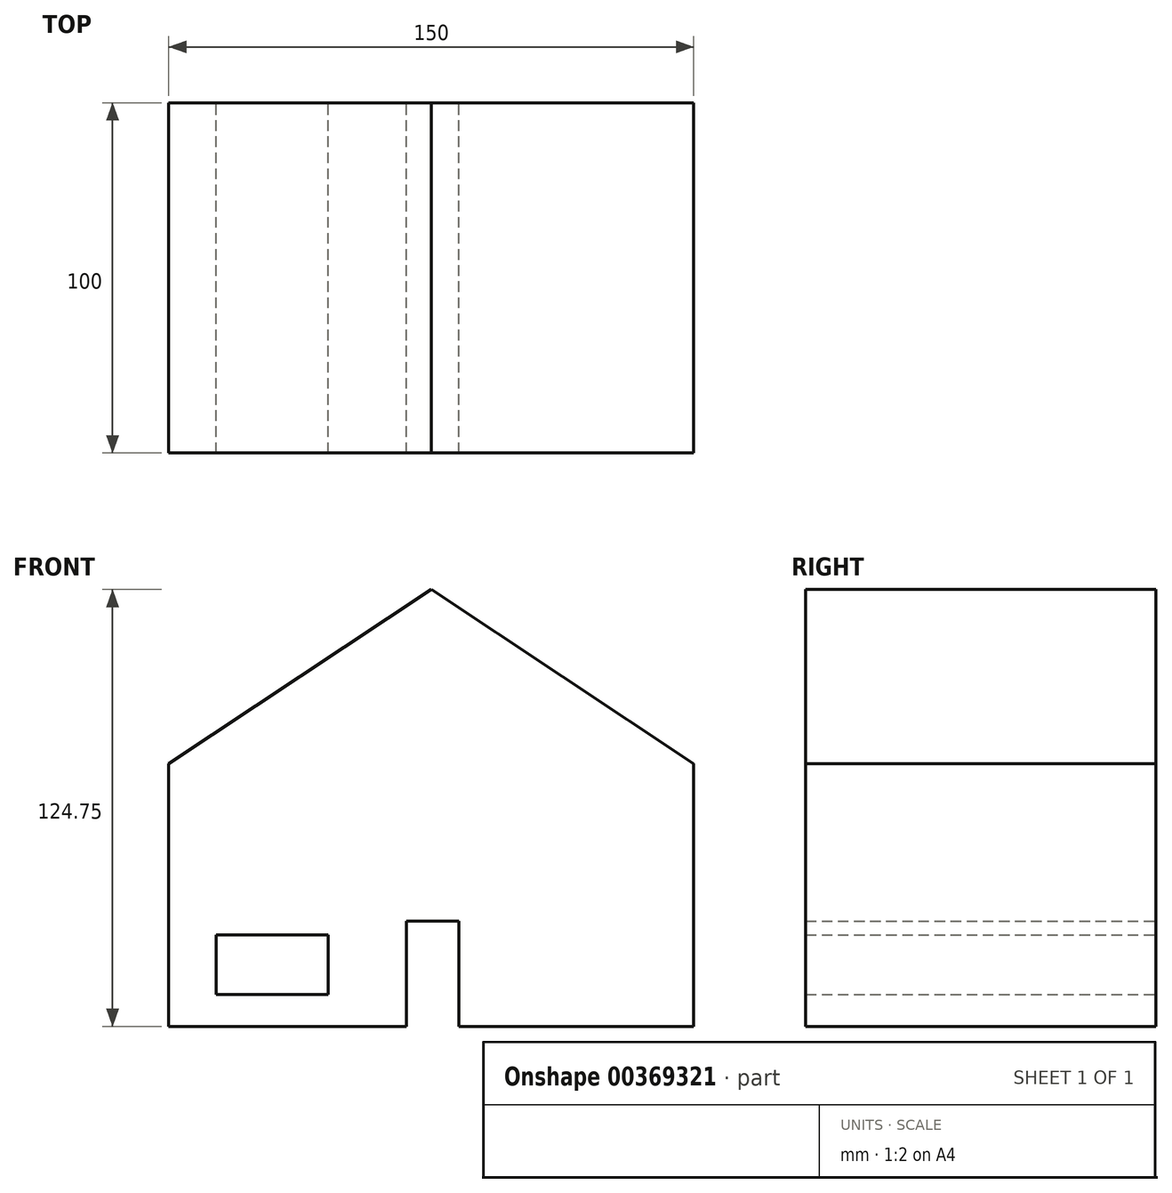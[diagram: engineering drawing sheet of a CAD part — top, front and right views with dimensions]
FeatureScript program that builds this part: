
annotation { "Feature Type Name" : "Feature", "Feature Type Description" : "" }
export const myFeature = defineFeature(function(context is Context, id is Id, definition is map)
    precondition{}
    {
        {
            var Q0;
            Q0=qCreatedBy(makeId("Front.planeOp"),FACE);
            var sketch = newSketch(context, id + "F0", { "sketchPlane" : qUnion([Q0])});
            skLineSegment(sketch, "E0.bottom", {"start": v(-75, -75) * mm, "end": v(75, -75) * mm});
            skLineSegment(sketch, "E0.top", {"start": v(-75, 0) * mm, "end": v(75, 0) * mm});
            skLineSegment(sketch, "E0.left", {"start": v(-75, -75) * mm, "end": v(-75, 0) * mm, "construction": true});
            skLineSegment(sketch, "E0.right", {"start": v(75, -75) * mm, "end": v(75, 0) * mm});
            skLineSegment(sketch, "E1", {"start": v(-75, 0) * mm, "end": v(0, 49.75) * mm});
            skLineSegment(sketch, "E2", {"start": v(0, 49.75) * mm, "end": v(75, 0) * mm});
            skLineSegment(sketch, "E3.left", {"start": v(-75, -37.5) * mm, "end": v(-75, -37.5) * mm});
            skLineSegment(sketch, "E3.right", {"start": v(75, -37.5) * mm, "end": v(75, -37.5) * mm});
            skLineSegment(sketch, "E4", {"start": v(-75, 0) * mm, "end": v(-75, -75) * mm});
            skLineSegment(sketch, "E5", {"start": v(-75, -37.5) * mm, "end": v(75, -37.5) * mm, "construction": true});
            skLineSegment(sketch, "E6.bottom", {"start": v(-7.1, -75) * mm, "end": v(7.9, -75) * mm});
            skLineSegment(sketch, "E6.top", {"start": v(-7.1, -45) * mm, "end": v(7.9, -45) * mm});
            skLineSegment(sketch, "E6.left", {"start": v(-7.1, -75) * mm, "end": v(-7.1, -45) * mm});
            skLineSegment(sketch, "E6.right", {"start": v(7.9, -75) * mm, "end": v(7.9, -45) * mm});
            skLineSegment(sketch, "E7.bottom", {"start": v(-61.5, -48.95) * mm, "end": v(-29.43, -48.95) * mm});
            skLineSegment(sketch, "E7.top", {"start": v(-61.5, -65.92) * mm, "end": v(-29.43, -65.92) * mm});
            skLineSegment(sketch, "E7.left", {"start": v(-61.5, -48.95) * mm, "end": v(-61.5, -65.92) * mm});
            skLineSegment(sketch, "E7.right", {"start": v(-29.43, -48.95) * mm, "end": v(-29.43, -65.92) * mm});
            skSolve(sketch);
        }
        {
            var Q0;
            Q0=makeQuery(id+"F0.imprint","IMPRINT",FACE,{"disambiguationData":[TD([[makeQuery(id+"F0.imprint","IMPRINT",EDGE,{"derivedFrom":sQuery(id+"F0.wireOp",EDGE,"E0.top")}),-1.0]])]});
            var Q1;
            Q1=makeQuery(id+"F0.imprint","IMPRINT",FACE,{"disambiguationData":[TD([[makeQuery(id+"F0.imprint","IMPRINT",EDGE,{"derivedFrom":sQuery(id+"F0.wireOp",EDGE,"E0.top")}),1.0]])]});
            var Q2;
            Q2=makeQuery(id+"F0.imprint","IMPRINT",FACE,{"disambiguationData":[TD([[makeQuery(id+"F0.imprint","IMPRINT",EDGE,{"derivedFrom":sQuery(id+"F0.wireOp",EDGE,"E6.bottom")}),1.0]])]});
            extrude(context, id + "F1", {"entities" : qUnion([Q0, Q1, Q2]), "depth" : 100 * mm});
        }
    });
